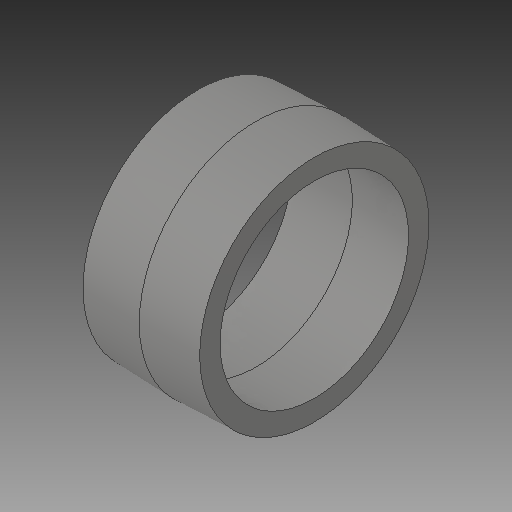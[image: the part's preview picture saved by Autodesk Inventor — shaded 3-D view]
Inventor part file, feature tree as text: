
AUTODESK INVENTOR PART (.ipt)
format: ipt  version: 2017 (Build 210142000, 142)  size: 118,784 bytes
history: native  units: in
note: dims shown in document units (in); Inventor stores cm internally (conversion verified against a paired STEP export)
features: revolve x1
ambient origin geometry x8: Origin, YZ Plane, XZ Plane, XY Plane, X Axis, Y Axis, Z Axis, Center Point
bodies: Solid1 (feature_tree)
feature tree (1):
  revolve  "Revolve1"  [1 undecoded]
note: 1 required parameter value undecoded (feature->parameter linkage not recoverable at this tier; creation-order binding heuristic only, values carry confidence <= 0.55)
